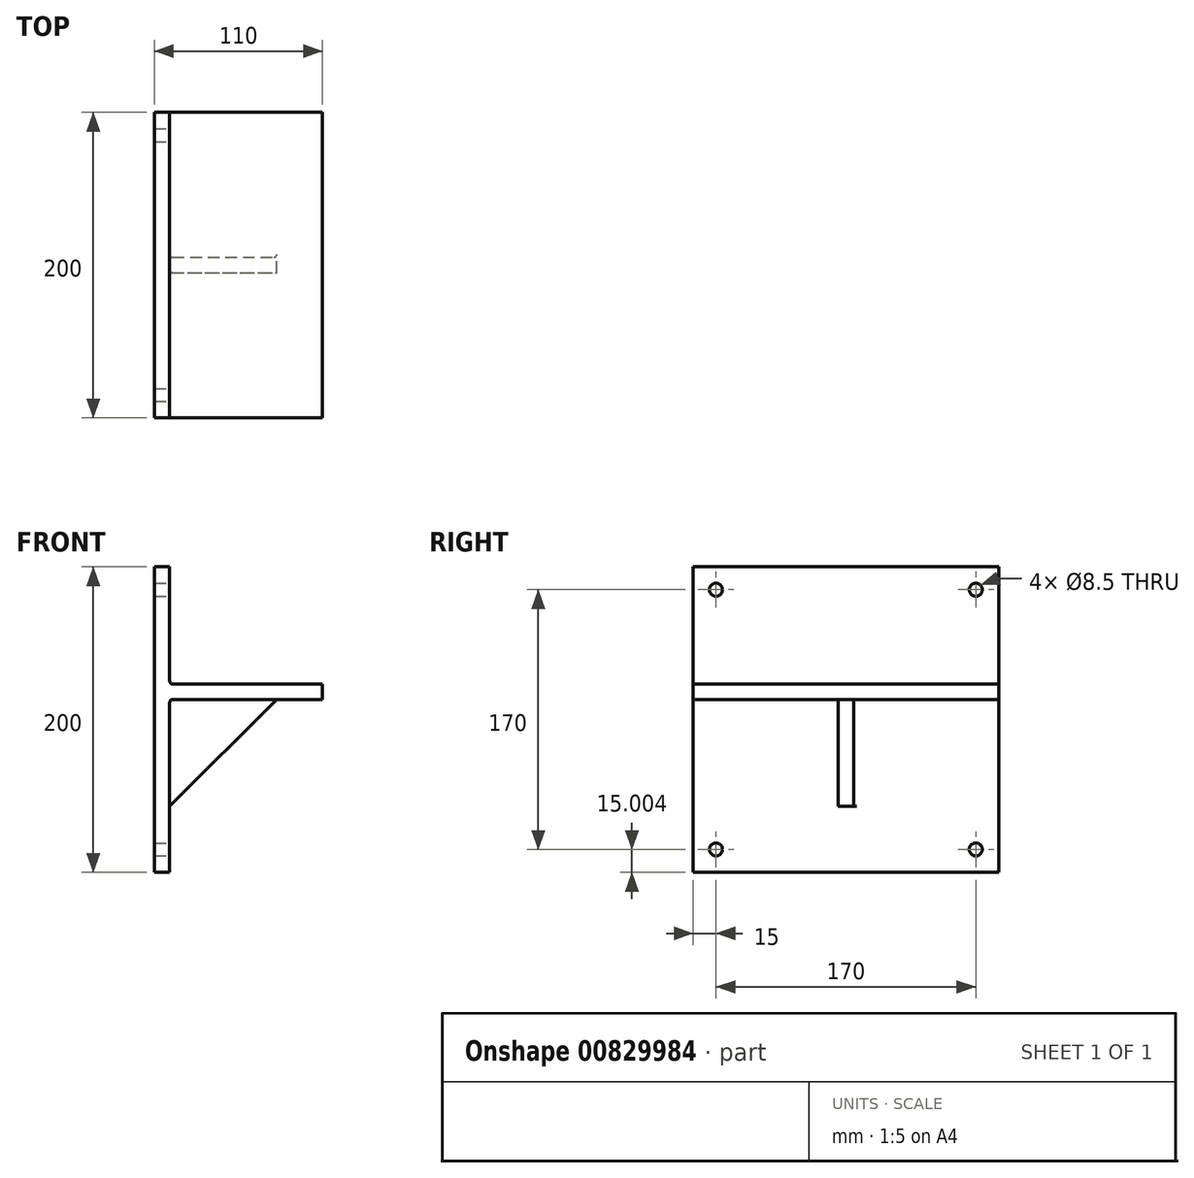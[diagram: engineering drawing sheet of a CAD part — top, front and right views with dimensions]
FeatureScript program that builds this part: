
annotation { "Feature Type Name" : "Feature", "Feature Type Description" : "" }
export const myFeature = defineFeature(function(context is Context, id is Id, definition is map)
    precondition{}
    {
        {
            var Q0;
            Q0=qCreatedBy(makeId("Front.planeOp"),FACE);
            var sketch = newSketch(context, id + "F0", { "sketchPlane" : qUnion([Q0])});
            skLineSegment(sketch, "E0", {"start": v(-43.83, -110.36) * mm, "end": v(-43.83, 89.64) * mm});
            skLineSegment(sketch, "E1", {"start": v(-43.83, 89.64) * mm, "end": v(-33.83, 89.64) * mm});
            skLineSegment(sketch, "E2", {"start": v(-43.83, -110.36) * mm, "end": v(-33.83, -110.36) * mm});
            skLineSegment(sketch, "E3", {"start": v(-33.83, -110.36) * mm, "end": v(-33.83, 2.84) * mm});
            skLineSegment(sketch, "E4", {"start": v(-33.83, 2.84) * mm, "end": v(66.17, 2.84) * mm});
            skLineSegment(sketch, "E5", {"start": v(66.17, 2.84) * mm, "end": v(66.17, 12.84) * mm});
            skLineSegment(sketch, "E6", {"start": v(66.17, 12.84) * mm, "end": v(-33.83, 12.84) * mm});
            skLineSegment(sketch, "E7", {"start": v(-33.83, 89.64) * mm, "end": v(-33.83, 12.84) * mm});
            skLineSegment(sketch, "E8", {"start": v(-33.83, 2.84) * mm, "end": v(-33.83, -67.16) * mm});
            skLineSegment(sketch, "E9", {"start": v(-33.83, 2.84) * mm, "end": v(36.17, 2.84) * mm});
            skLineSegment(sketch, "E10", {"start": v(-33.83, -67.16) * mm, "end": v(36.17, 2.84) * mm});
            skSolve(sketch);
        }
        {
            var Q0;
            {var subQ0=sQuery(id+"F0.wireOp",EDGE,"E10");Q0=makeQuery(id+"F0.imprint","IMPRINT",FACE,{"disambiguationData":[TD([[makeQuery(id+"F0.imprint","IMPRINT",EDGE,{"derivedFrom":subQ0}),1.0]])]});}
            extrude(context, id + "F1", {"entities" : qUnion([Q0]), "depth" : 5 * mm, "offsetDistance" : 25 * mm});
        }
        {
            var Q0;
            {var subQ0=sQuery(id+"F0.wireOp",EDGE,"E10");Q0=makeQuery(id+"F0.imprint","IMPRINT",FACE,{"disambiguationData":[TD([[makeQuery(id+"F0.imprint","IMPRINT",EDGE,{"derivedFrom":subQ0}),1.0]])]});}
            extrude(context, id + "F2", {"entities" : qUnion([Q0]), "operationType" : NewBodyOperationType.ADD, "oppositeDirection" : true, "depth" : 5 * mm, "offsetDistance" : 25 * mm});
        }
        {
            var Q0;
            Q0=makeQuery(id+"F0.imprint","IMPRINT",FACE,{"disambiguationData":[TD([[makeQuery(id+"F0.imprint","IMPRINT",EDGE,{"derivedFrom":sQuery(id+"F0.wireOp",EDGE,"E0")}),-1.0]])]});
            extrude(context, id + "F3", {"entities" : qUnion([Q0]), "operationType" : NewBodyOperationType.ADD, "depth" : 100 * mm, "offsetDistance" : 25 * mm});
        }
        {
            var Q0;
            Q0=makeQuery(id+"F3.opExtrude","CAP_FACE",FACE,{"disambiguationData":[OSD([sQuery(id+"F0.wireOp",EDGE,"E0"),sQuery(id+"F0.wireOp",EDGE,"E1"),sQuery(id+"F0.wireOp",EDGE,"E2"),sQuery(id+"F0.wireOp",EDGE,"E3"),sQuery(id+"F0.wireOp",EDGE,"E4"),sQuery(id+"F0.wireOp",EDGE,"E5"),sQuery(id+"F0.wireOp",EDGE,"E6"),sQuery(id+"F0.wireOp",EDGE,"E7")])],"isStart":true});
            extrude(context, id + "F4", {"entities" : qUnion([Q0]), "operationType" : NewBodyOperationType.ADD, "depth" : 100 * mm, "offsetDistance" : 25 * mm});
        }
        {
            var Q0;
            {var subQ0=sQuery(id+"F0.wireOp",EDGE,"E3");Q0=makeQuery(id+"F4.boolean.opBoolean","MERGE",FACE,{"derivedFrom":[makeQuery(id+"F3.opExtrude","SWEPT_FACE",FACE,{"disambiguationData":[OSD([subQ0])]}),makeQuery(id+"F4.opExtrude","SWEPT_FACE",FACE,{"disambiguationData":[OSD([subQ0])]})]});}
            var sketch = newSketch(context, id + "F5", { "sketchPlane" : qUnion([Q0])});
            skCircle(sketch, "E11", {"center": v(-85, 74.64) * mm, "radius": 4.25 * mm});
            skCircle(sketch, "E12", {"center": v(85, 74.64) * mm, "radius": 4.25 * mm});
            skCircle(sketch, "E13", {"center": v(-85, -95.36) * mm, "radius": 4.25 * mm});
            skCircle(sketch, "E14", {"center": v(85, -95.36) * mm, "radius": 4.25 * mm});
            skSolve(sketch);
        }
        {
            var Q0;
            Q0=makeQuery(id+"F5.imprint","IMPRINT",FACE,{"disambiguationData":[TD([[makeQuery(id+"F5.imprint","IMPRINT",EDGE,{"derivedFrom":sQuery(id+"F5.wireOp",EDGE,"E13")}),1.0]])]});
            var Q1;
            Q1=makeQuery(id+"F5.imprint","IMPRINT",FACE,{"disambiguationData":[TD([[makeQuery(id+"F5.imprint","IMPRINT",EDGE,{"derivedFrom":sQuery(id+"F5.wireOp",EDGE,"E14")}),1.0]])]});
            var Q2;
            Q2=makeQuery(id+"F5.imprint","IMPRINT",FACE,{"disambiguationData":[TD([[makeQuery(id+"F5.imprint","IMPRINT",EDGE,{"derivedFrom":sQuery(id+"F5.wireOp",EDGE,"E12")}),1.0]])]});
            var Q3;
            Q3=makeQuery(id+"F5.imprint","IMPRINT",FACE,{"disambiguationData":[TD([[makeQuery(id+"F5.imprint","IMPRINT",EDGE,{"derivedFrom":sQuery(id+"F5.wireOp",EDGE,"E11")}),1.0]])]});
            extrude(context, id + "F6", {"entities" : qUnion([Q0, Q1, Q2, Q3]), "operationType" : NewBodyOperationType.REMOVE, "oppositeDirection" : true, "depth" : 10 * mm, "offsetDistance" : 25 * mm});
        }
        {
            var Q0;
            Q0=makeQuery(id+"F3.opExtrude","SWEPT_EDGE",EDGE,{"disambiguationData":[OSD([sQuery(id+"F0.wireOp",EDGE,"E3"),sQuery(id+"F0.wireOp",EDGE,"E4")])]});
            var Q1;
            Q1=makeQuery(id+"F4.opExtrude","SWEPT_EDGE",EDGE,{"disambiguationData":[OSD([sQuery(id+"F0.wireOp",EDGE,"E3"),sQuery(id+"F0.wireOp",EDGE,"E4")])]});
            var Q2;
            Q2=makeQuery(id+"F2.opExtrude","CAP_EDGE",EDGE,{"disambiguationData":[OSD([sQuery(id+"F0.wireOp",EDGE,"E4")])],"isStart":false});
            var Q3;
            Q3=makeQuery(id+"F2.opExtrude","CAP_EDGE",EDGE,{"disambiguationData":[OSD([sQuery(id+"F0.wireOp",EDGE,"E3")])],"isStart":false});
            var Q4;
            Q4=makeQuery(id+"F1.opExtrude","CAP_EDGE",EDGE,{"disambiguationData":[OSD([sQuery(id+"F0.wireOp",EDGE,"E4")])],"isStart":false});
            var Q5;
            Q5=makeQuery(id+"F1.opExtrude","CAP_EDGE",EDGE,{"disambiguationData":[OSD([sQuery(id+"F0.wireOp",EDGE,"E3")])],"isStart":false});
            var Q6;
            {var subQ0=sQuery(id+"F0.wireOp",EDGE,"E7");var subQ1=sQuery(id+"F0.wireOp",EDGE,"E6");Q6=makeQuery(id+"F4.boolean.opBoolean","MERGE",EDGE,{"derivedFrom":[makeQuery(id+"F3.opExtrude","SWEPT_EDGE",EDGE,{"disambiguationData":[OSD([subQ1,subQ0])]}),makeQuery(id+"F4.opExtrude","SWEPT_EDGE",EDGE,{"disambiguationData":[OSD([subQ1,subQ0])]})]});}
            fillet(context, id + "F7", {"entities" : qUnion([Q0, Q1, Q2, Q3, Q4, Q5, Q6]), "radius" : 2 * mm, "tangentPropagation" : true, "allowEdgeOverflow" : false});
        }
    });
